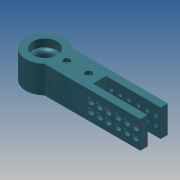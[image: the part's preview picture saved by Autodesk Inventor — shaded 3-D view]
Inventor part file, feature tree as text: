
AUTODESK INVENTOR PART (.ipt)
format: ipt  version: 2013 (Build 170138000, 138)  size: 296,448 bytes
history: native  units: mm
features: extrude x10, sketch x10, pattern_linear x2, fillet x1
ambient origin geometry x8: Origin, YZ Plane, XZ Plane, XY Plane, X Axis, Y Axis, Z Axis, Center Point
bodies: Solid1 (feature_tree)
feature tree (23):
  extrude  "Extrusion1"  Depth=12.6mm
  extrude  "Extrusion2"  Depth=8.5mm
  extrude  "Extrusion3"  Depth=22.0mm
  extrude  "Extrusion4"  Depth=20.0mm
  extrude  "Extrusion5"  Depth=7.0mm TaperAngle=0.0deg
  extrude  "Extrusion6"  Depth=3.5mm
  fillet  "Fillet1"  Radius=35.0mm
  extrude  "Extrusion7"  Depth=6.0mm
  extrude  "Extrusion8"  Depth=8.0mm TaperAngle=0.0deg
  extrude  "Extrusion9"  Depth=12.0mm
  extrude  "Extrusion10"  Depth=50.0mm
  pattern_linear  "Rectangular Pattern1"  Spacing1=10.0mm  [1 undecoded]
  pattern_linear  "Rectangular Pattern2"  Spacing1=12.5mm  [1 undecoded]
  sketch  "Sketch1"  dims[d0=150.0mm d2=12.6mm]
  sketch  "Sketch2"  dims[d3=15.0mm d4=8.5mm]
  sketch  "Sketch4"  dims[d5=25.0mm d6=0.0mm d7=22.0mm]
  sketch  "Sketch5"  dims[d9=7.0mm d10=0.0mm d16=20.0mm]
  sketch  "Sketch6"  dims[d17=40.0mm d18=7.0mm d19=0.0mm]
  sketch  "Sketch7"  dims[d21=3.0mm d22=0.0mm d23=3.5mm d24=35.0mm]
  sketch  "Sketch8"  dims[d26=10.0mm d27=0.0mm d28=6.0mm]
  sketch  "Sketch9"  dims[d30=14.0mm d32=8.0mm d33=0.0mm]
  sketch  "Sketch10"  dims[d34=3.5mm d35=12.0mm]
  sketch  "Sketch11"  dims[d37=50.0mm d38=50.0mm d39=10.0mm d40=0.0mm d41=12.5mm d42=8.0mm d43=3.5mm d44=10.0mm d45=0.0mm d46=6.0mm d48=3.0mm d49=0.0mm d50=5.5mm d51=4.0mm d52=0.0mm d53=30.0mm d55=8.0mm d56=20.0mm d58=8.0mm d59=20.0mm d61=25.0mm]
note: 2 required parameter values undecoded (feature->parameter linkage not recoverable at this tier; creation-order binding heuristic only, values carry confidence <= 0.55)
